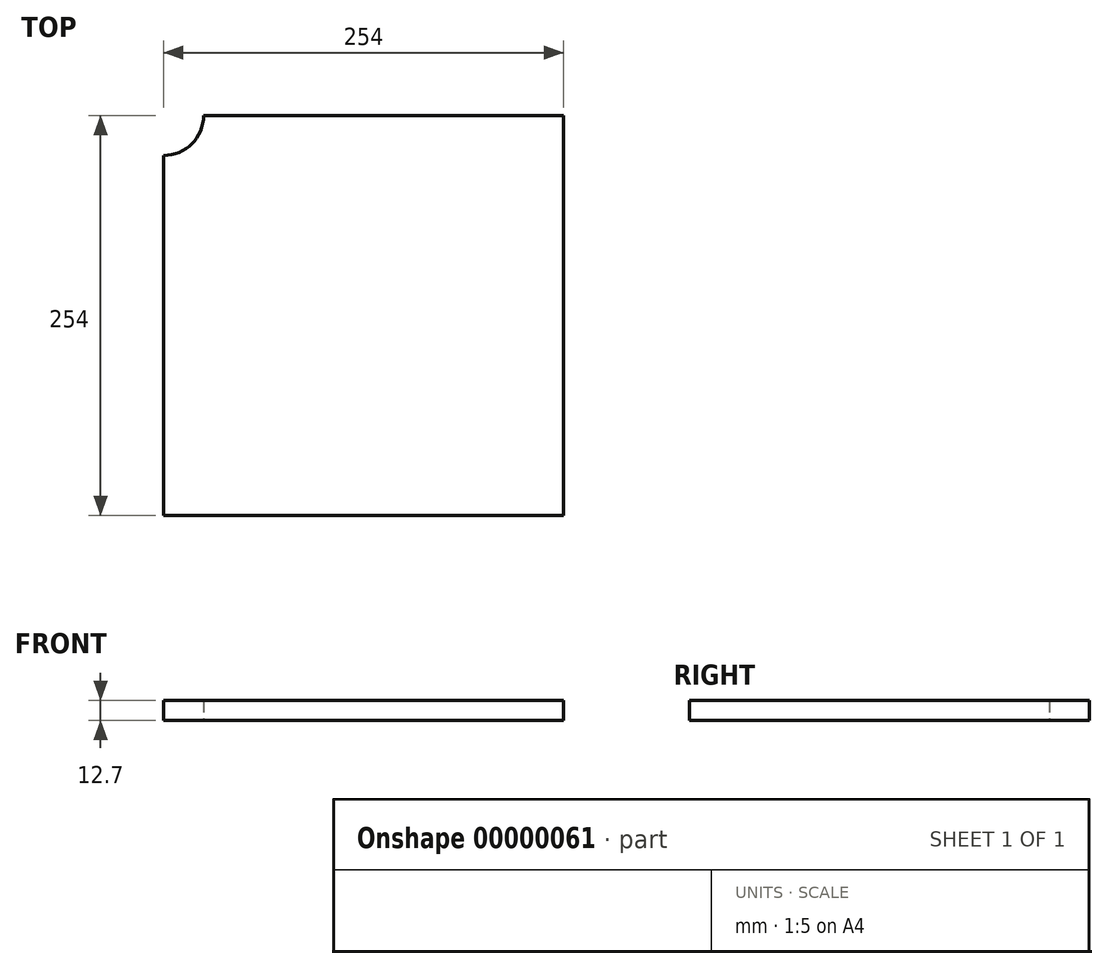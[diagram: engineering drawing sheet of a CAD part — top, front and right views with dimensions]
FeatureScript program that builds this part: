
annotation { "Feature Type Name" : "Feature", "Feature Type Description" : "" }
export const myFeature = defineFeature(function(context is Context, id is Id, definition is map)
    precondition{}
    {
        {
            var Q0;
            Q0=qCreatedBy(makeId("Top.planeOp"),FACE);
            var sketch = newSketch(context, id + "F0", { "sketchPlane" : qUnion([Q0])});
            skLineSegment(sketch, "E0.bottom", {"start": v(0, 0) * mm, "end": v(254, 0) * mm});
            skLineSegment(sketch, "E0.top", {"start": v(0, -254) * mm, "end": v(254, -254) * mm});
            skLineSegment(sketch, "E0.left", {"start": v(0, 0) * mm, "end": v(0, -254) * mm});
            skLineSegment(sketch, "E0.right", {"start": v(254, 0) * mm, "end": v(254, -254) * mm});
            skCircle(sketch, "E1", {"center": v(0, 0) * mm, "radius": 25.4 * mm});
            skSolve(sketch);
        }
        {
            var Q0;
            {var subQ6=sQuery(id+"F0.wireOp",EDGE,"E0.top");Q0=makeQuery(id+"F0.imprint","IMPRINT",FACE,{"disambiguationData":[TD([[makeQuery(id+"F0.imprint","IMPRINT",EDGE,{"derivedFrom":subQ6}),1.0]])]});}
            extrude(context, id + "F1", {"entities" : qUnion([Q0]), "depth" : 12.7 * mm});
        }
    });
